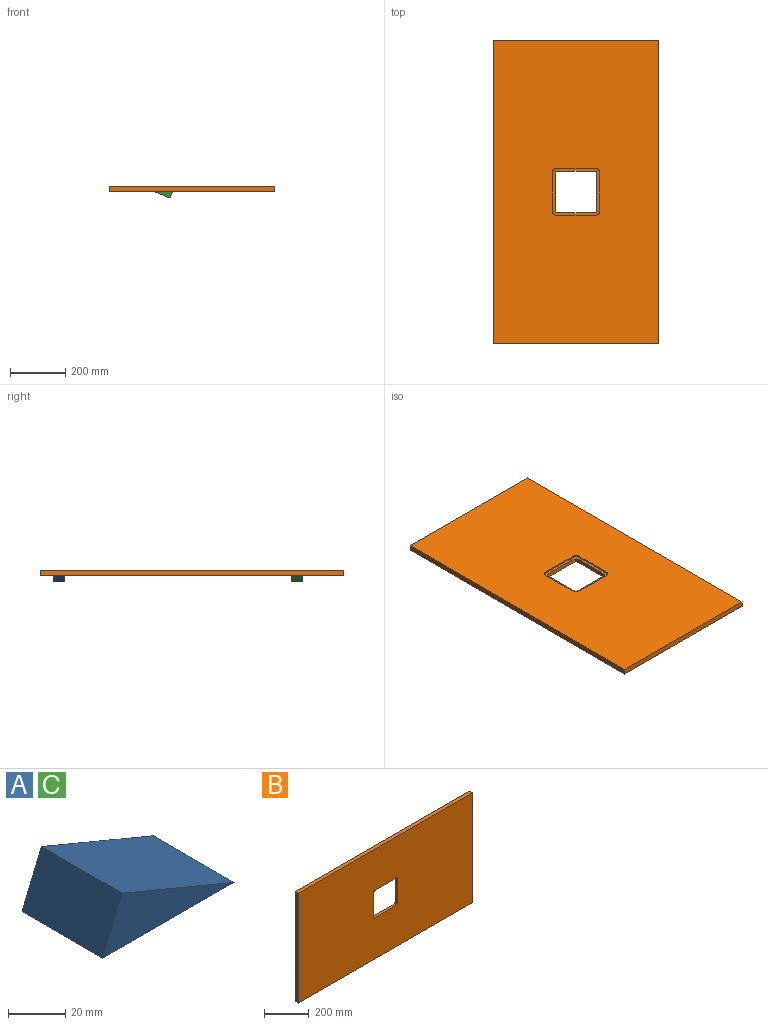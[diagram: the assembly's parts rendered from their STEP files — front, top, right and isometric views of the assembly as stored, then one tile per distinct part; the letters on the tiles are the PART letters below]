
ASSEMBLY  parts=3 mates=2
PART A: 5 faces, bbox 65x40x23.1 mm
  f0: plane 65x40mm, normal (0,0,-1), area 2600mm2, adj f1,f2,f3,f4
  f1: plane 55.38x40mm, normal (0.38,0,0.92), area 2400mm2, adj f0,f2,f3,f4
  f2: plane 40x23.08mm, normal (-0.92,0,0.38), area 1000mm2, adj f0,f1,f3,f4
  f3: plane 65x23.08mm, normal (0,-1,0), area 750mm2, adj f0,f1,f2
  f4: plane 65x23.08mm, normal (0,1,0), area 750mm2, adj f0,f1,f2
PART B: 23 faces, bbox 1100x20x600 mm
  f0: plane 140x15mm, normal (1,0,0), area 2100mm2, adj f1,f7,f8,f22
  f1: cylinder r=5mm len=15mm, axis (0,1,0), area 117.8mm2, adj f0,f2,f8,f22
  f2: plane 140x15mm, normal (0,0,-1), area 2100mm2, adj f1,f3,f8,f22
  f3: cylinder r=5mm len=15mm, axis (0,1,0), area 117.8mm2, adj f2,f4,f8,f22
  f4: plane 140x15mm, normal (-1,0,0), area 2100mm2, adj f3,f5,f8,f22
  f5: cylinder r=5mm len=15mm, axis (0,1,0), area 117.8mm2, adj f4,f6,f8,f22
  f6: plane 140x15mm, normal (0,0,1), area 2100mm2, adj f5,f7,f8,f22
  f7: cylinder r=5mm len=15mm, axis (0,1,0), area 117.8mm2, adj f0,f6,f8,f22
  f8: plane 1100x600mm, normal (0,-1,0), area 637521.5mm2, adj f0,f1,f2,f3,f4,f5,f6,f7
  f9: plane 1100x600mm, normal (0,1,0), area 631293.1mm2, adj f10,f11,f12,f13,f14,f15,f16,f17
  f10: plane 600x20mm, normal (1,0,0), area 12000mm2, adj f8,f9,f11,f13
  f11: plane 1100x20mm, normal (0,0,1), area 22000mm2, adj f8,f9,f10,f12
  f12: plane 600x20mm, normal (-1,0,0), area 12000mm2, adj f8,f9,f11,f13
  f13: plane 1100x20mm, normal (0,0,-1), area 22000mm2, adj f8,f9,f10,f12
  f14: plane 140x5mm, normal (0,0,1), area 700mm2, adj f9,f15,f21,f22
  f15: cylinder r=15mm len=15mm, axis (0,1,0), area 117.8mm2, adj f9,f14,f16,f22
  f16: plane 140x5mm, normal (1,0,0), area 700mm2, adj f9,f15,f17,f22
  f17: cylinder r=15mm len=15mm, axis (0,1,0), area 117.8mm2, adj f9,f16,f18,f22
  f18: plane 140x5mm, normal (0,0,-1), area 700mm2, adj f9,f17,f19,f22
  f19: cylinder r=15mm len=15mm, axis (0,1,0), area 117.8mm2, adj f9,f18,f20,f22
  f20: plane 140x5mm, normal (-1,0,0), area 700mm2, adj f9,f19,f21,f22
  f21: cylinder r=15mm len=15mm, axis (0,1,0), area 117.8mm2, adj f9,f14,f20,f22
  f22: plane 170x170mm, normal (0,1,0), area 6228.3mm2, adj f0,f1,f2,f3,f4,f5,f6,f7
PART C: same geometry as A
PLACE A rot(axis=(0,1,0),180deg) t=(599.92,1337.68,426.76)mm
PLACE B rot(axis=(0.58,0.58,0.58),120deg) t=(702.42,837.68,459.7)mm
PLACE C rot(axis=(0,1,0),180deg) t=(599.92,477.68,426.76)mm
MATE fastened A.f0 <-> B.f8  axis (0,0,1) through (632.42,1317.68,439.7)mm
MATE fastened C.f0 <-> B.f8  axis (0,0,1) through (632.42,457.68,439.7)mm
